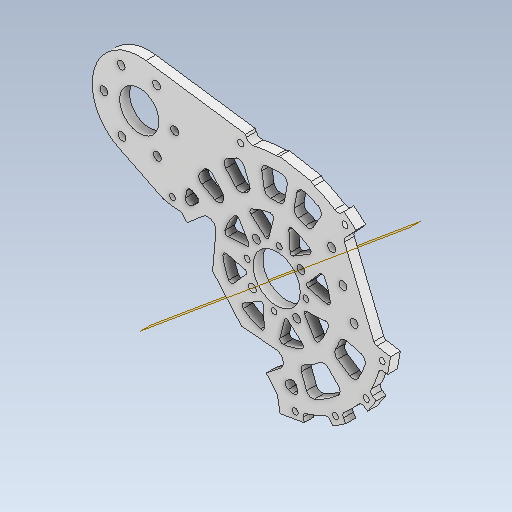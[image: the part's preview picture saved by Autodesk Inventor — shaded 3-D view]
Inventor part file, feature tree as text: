
AUTODESK INVENTOR PART (.ipt)
format: ipt  version: 2020 (Build 240168000, 168)  size: 1,434,624 bytes
history: native  units: mm
features: reference x16, sketch x13, extrude x12, other x8, projected_geometry x7, thicken_offset x4, fillet x4, mirror x2, shell x2, hole x1, pattern_circular x1, plane x1
ambient origin geometry x8: Origin, YZ Plane, XZ Plane, XY Plane, X Axis, Y Axis, Z Axis, Center Point
bodies: Solid1 (feature_tree)
feature tree (71):
  extrude  "Extrusion1"  Depth=5.0mm TaperAngle=0.0deg
  hole  "Hole1"  [1 undecoded]
  extrude  "Extrusion2"  Depth=5.0mm
  extrude  "Extrusion3"  Depth=4.0mm
  thicken_offset  "Thicken1"
  pattern_circular  "Circular Pattern1"  Count=8 Angle=360.0deg
  extrude  "Extrusion4"  Depth=8.0mm
  plane  "Work Plane1"
  mirror  "Mirror1"
  extrude  "Extrusion5"  Depth=5.0mm TaperAngle=0.0deg
  mirror  "Mirror2"
  extrude  "Extrusion6"  Depth=95.0mm
  extrude  "Extrusion7"  Depth=4.363323mm
  extrude  "Extrusion8"  Depth=4.363323mm
  extrude  "Extrusion9"  Depth=5.0mm
  fillet  "Fillet1"  Radius=2.094395mm
  fillet  "Fillet2"  Radius=6.981317mm
  fillet  "Fillet3"  Radius=1.745329mm
  fillet  "Fillet4"  Radius=5.0mm
  extrude  "Extrusion10"  Depth=5.0mm
  extrude  "Extrusion11"  Depth=5.0mm
  thicken_offset  "Thicken2"
  thicken_offset  "Thicken3"
  thicken_offset  "Thicken4"
  extrude  "Extrusion12"  Depth=5.0mm
  sketch  "Sketch1"  dims[d0=60.0mm d1=5.0mm d2=0.0mm]
  reference  "Reference1"
  reference  "Reference2"
  reference  "Reference3"
  sketch  "Sketch2"  dims[d3=3.1mm d4=6.0mm d5=4.0mm d6=2.0mm d7=90.0deg d8=17.0mm d9=0.0mm d10=60.0mm]
  reference  "Reference4"
  reference  "Reference5"
  reference  "Reference6"
  reference  "Reference7"
  reference  "Reference8"
  reference  "Reference9"
  reference  "Reference10"
  sketch  "Sketch3"  dims[d11=5.0mm d12=0.0mm d13=60.0mm]
  sketch  "Sketch5"  dims[d21=15.0mm d22=8.0mm]
  reference  "Reference11"
  reference  "Reference12"
  reference  "Reference13"
  reference  "Reference14"
  sketch  "Sketch6"  dims[d23=5.0mm d24=0.0mm d25=5.0mm d26=0.0mm]
  projected_geometry  "Projected Loop1"
  sketch  "Sketch7"  dims[d27=68.0mm d28=95.0mm]
  projected_geometry  "Projected Loop2"
  sketch  "Sketch8"  dims[d29=1.745329mm d30=4.363323mm]
  projected_geometry  "Projected Loop3"
  sketch  "Sketch9"  dims[d31=2.094395mm d32=4.363323mm]
  projected_geometry  "Projected Loop4"
  sketch  "Sketch10"  dims[d33=1.745329mm d34=6.981317mm d35=2.094395mm d36=6.981317mm d37=1.745329mm d39=5.0mm d40=0.0mm]
  projected_geometry  "Projected Loop5"
  sketch  "Sketch11"  dims[d41=5.0mm d42=5.0mm]
  projected_geometry  "Projected Loop6"
  sketch  "Sketch12"  dims[d43=5.0mm d44=0.0mm d45=0.872665mm]
  projected_geometry  "Projected Loop7"
  reference  "Reference15"
  sketch  "Sketch13"  dims[d46=5.0mm d47=0.0mm d48=5.0mm d49=5.0mm d50=10.0mm d51=5.0mm d52=5.0mm d53=10.0mm d54=5.0mm d55=0.0mm d56=3.0mm d57=3.0mm d58=2.0mm d59=2.0mm d60=3.0mm d61=15.0mm d62=4.1mm d63=4.1mm d64=15.0mm d65=4.1mm d66=10.0mm d67=0.0mm d68=80.0mm d69=18.0mm d70=30.0deg d71=4.0mm d72=60.0mm d74=360.0deg d76=48.0mm d77=5.0mm d78=0.0mm d79=2.0mm d80=2.0mm d81=2.0mm d82=2.0mm d83=2.0mm d84=1.0mm d85=20.0mm d86=10.0mm d87=0.0mm]
  reference  "Reference16"
  parser-record x2  (decoder bookkeeping rows leaked as tree rows — omitted from the tree; the rows remain in map.json)
  other  "reducer_2.iam"
  other  "90_motor:1"
  other  "90motor_base:1"
  shell  "shell_5:1"  Thickness=5.0mm
  shell  "shell_3:1"  Thickness=10.0mm
  sketch  "Sketch4"  dims[d14=5.0mm d15=0.0mm d16=4.0mm d17=1.0mm d18=80.0mm d19=360.0deg]
  other  "reducer_3.iam"
  other  "motor_h_4:1"
  other  "motor_h_5_m:1"
note: 1 required parameter value undecoded (feature->parameter linkage not recoverable at this tier; creation-order binding heuristic only, values carry confidence <= 0.55)
note: 2 file-system paths scrubbed to <path> (originals preserved in map.json)
